# Revit family: Genie_ElectricScissorLift_(GS-4046)
name_source: partatom
category: Site
units: mm (PartAtom-declared; Revit-internal decimal feet)

## family parameters
Always vertical = Yes
Cut with Voids When Loaded = No
OmniClass Number = 23.50.05.14.11
OmniClass Title = Scissors Lifts
Part Type = Normal
Round Connector Dimension = Use Diameter
Shared = No
Work Plane-Based = No

## types (1)
- GS-4046 Electric Scissor Lift
    Assembly Code = E1030900
    AssetType = Moveable
    BIMObjectName = Genie_ElectricScissorLift_(GS-4046)
    BaseHeight = 632 mm
    Blue = Steel, Paint Finish, Blue, Genie
    ClassificationName = Uniclass2015
    ClassificationValue = TE_30_30_60_60
    Clearance = ClearanceZone
    Color = Blue
    Cost = 0 $
    Description = GS-4046 Electric Scissor Lift
    DocumentationCertificates = https://www.bimstore.co
    DocumentationInstallationGuide = https://www.bimstore.co
    DocumentationLiterature = https://www.bimstore.co
    DocumentationMaintenance = https://www.bimstore.co
    DocumentationTechnical = https://www.bimstore.co
    DurationUnit = Years
    ExpectedLife = 0
    Grey = Steel, Paint Finish, Grey, Genie
    HeightStowed = 0 mm  [stored 0 ft]
    IfcExportAs = IfcTransportElement
    IfcExportType = IfcTransportElementType
    Keynote = X
    LengthStowed = 0 mm  [stored 0 ft]
    LiftCapacityMaximum = 0.00 kg
    Manufacturer = Genie
    ManufacturerName = Genie
    Model = GS-4046 Electric Scissor Lift
    ModelNumber = GS-4046
    ModelReference = Electric Scissor Lift
    NBSDescription = Scissor lifts
    NBSObjectName = Genie - Scissor lifts
    NominalDepth = 0 mm  [stored 0 ft]
    NominalHeight = 0 mm  [stored 0 ft]
    NominalLength = 0 mm  [stored 0 ft]
    ProductionYear = 2023
    ScissorPosition = 1013 mm
    SpareParts = https://www.genielift.com
    Tire = Rubber, Tire, Grey
    TurningRadiusInside = 0 mm  [stored 0 ft]
    TurningRadiusOutside = 0 mm  [stored 0 ft]
    Type Comments = GS-4046 Electric Scissor Lift
    TypeName = GS-4046 Electric Scissor Lift
    URL = https://www.genielift.com
    WarrantyDurationLabor = 0
    WarrantyDurationParts = 0
    WarrantyDurationUnit = Years
    WarrantyGuarantorLabor = https://www.genielift.com
    WarrantyGuarantorParts = https://www.genielift.com
    Weight = 0.00 kg
    White = White
    Width = 0 mm  [stored 0 ft]
    _BSBibleVersion = 17
    _BimSpecGuid = 0
    _CurrentRevision = 1
    _DistributedBy = https://www.bimstore.co
    _ObjectUserGuide = https://www.bimstore.co

note: [stored X ft] marks values corroborated as IEEE doubles in the binary element streams (Revit-internal decimal feet)

## geometry (parser evidence)
native form markers: Sweep x15
no freeform markers — native parametric forms only
